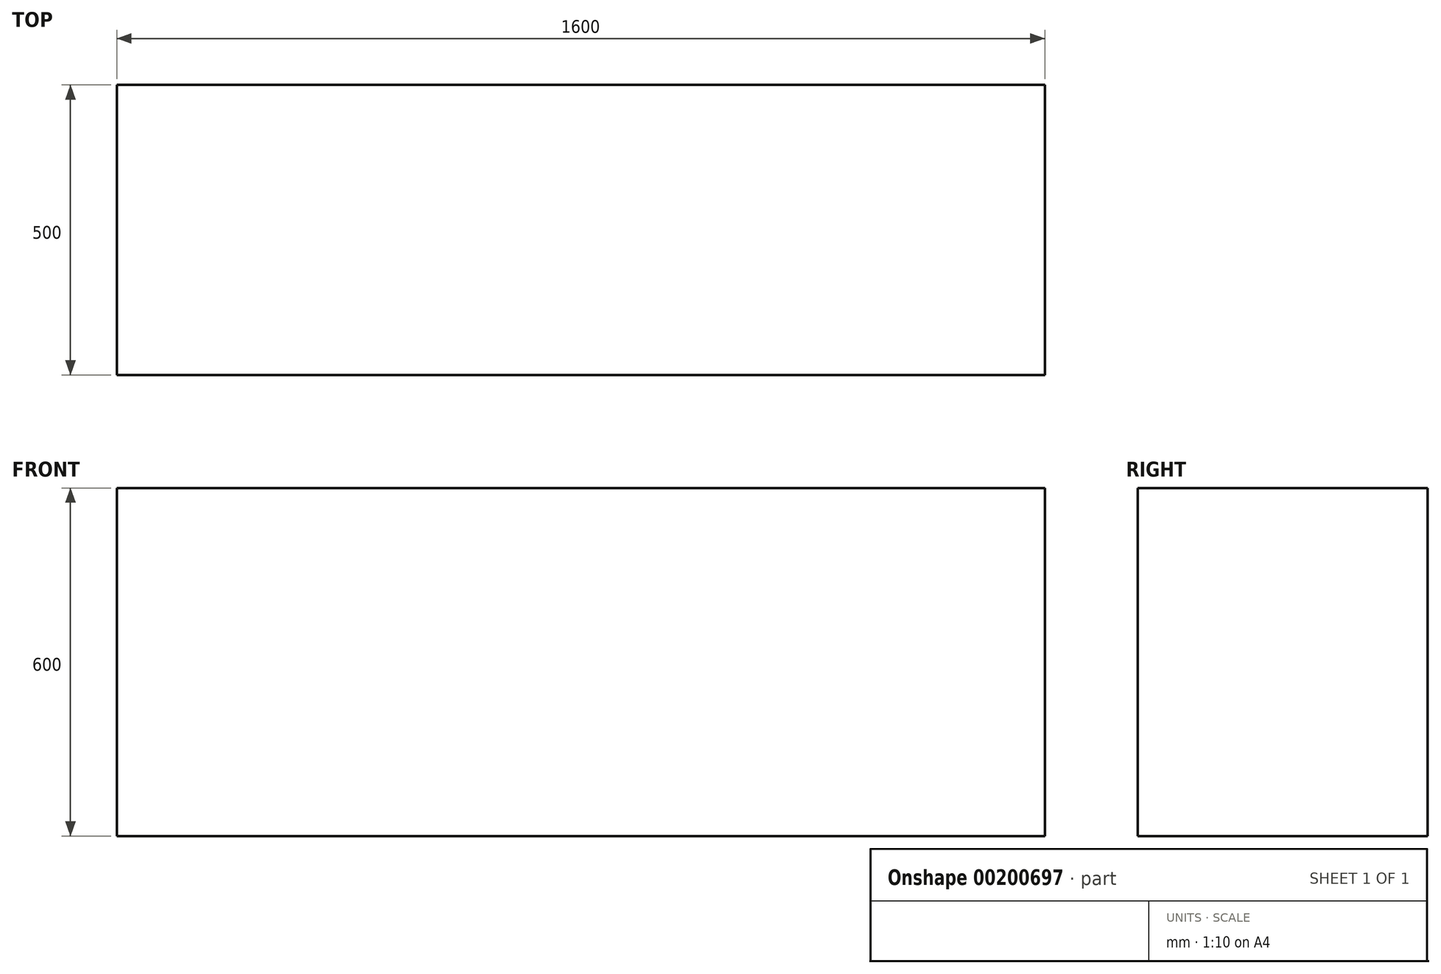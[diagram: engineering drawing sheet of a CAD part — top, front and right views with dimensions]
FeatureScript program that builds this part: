
annotation { "Feature Type Name" : "Feature", "Feature Type Description" : "" }
export const myFeature = defineFeature(function(context is Context, id is Id, definition is map)
    precondition{}
    {
        {
            var Q0;
            Q0=qCreatedBy(makeId("Front.planeOp"),FACE);
            var sketch = newSketch(context, id + "F0", { "sketchPlane" : qUnion([Q0])});
            skLineSegment(sketch, "E0.bottom", {"start": v(0, 0) * mm, "end": v(1600, 0) * mm});
            skLineSegment(sketch, "E0.top", {"start": v(0, 600) * mm, "end": v(1600, 600) * mm});
            skLineSegment(sketch, "E0.left", {"start": v(0, 0) * mm, "end": v(0, 600) * mm});
            skLineSegment(sketch, "E0.right", {"start": v(1600, 0) * mm, "end": v(1600, 600) * mm});
            skSolve(sketch);
        }
        {
            var Q0;
            Q0=qSketchRegion(id+"F0",true);
            extrude(context, id + "F1", {"entities" : qUnion([Q0]), "depth" : 500 * mm});
        }
    });
